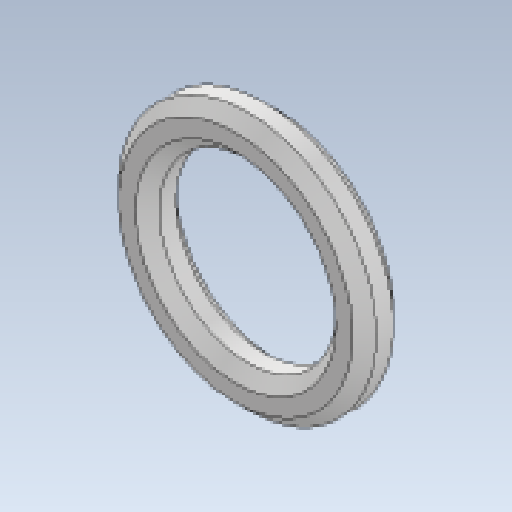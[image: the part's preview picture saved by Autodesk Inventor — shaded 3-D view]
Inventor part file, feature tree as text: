
AUTODESK INVENTOR PART (.ipt)
format: ipt  version: 2023 (Build 270158030, 158C)  size: 112,128 bytes
history: native  units: mm
features: extrude x1, chamfer x1, sketch x1
ambient origin geometry x8: Origin, YZ Plane, XZ Plane, XY Plane, X Axis, Y Axis, Z Axis, Center Point
bodies: Solid1 (feature_tree)
feature tree (3):
  extrude  "Extrusion1"  Depth=1.7mm
  chamfer  "Chamfer1"  Distance=1.7mm
  sketch  "Sketch1"  dims[d0=10.8mm d1=1.7mm d2=1.7mm d3=0.0mm d4=0.5mm d5=2.0mm d6=45.0deg]
